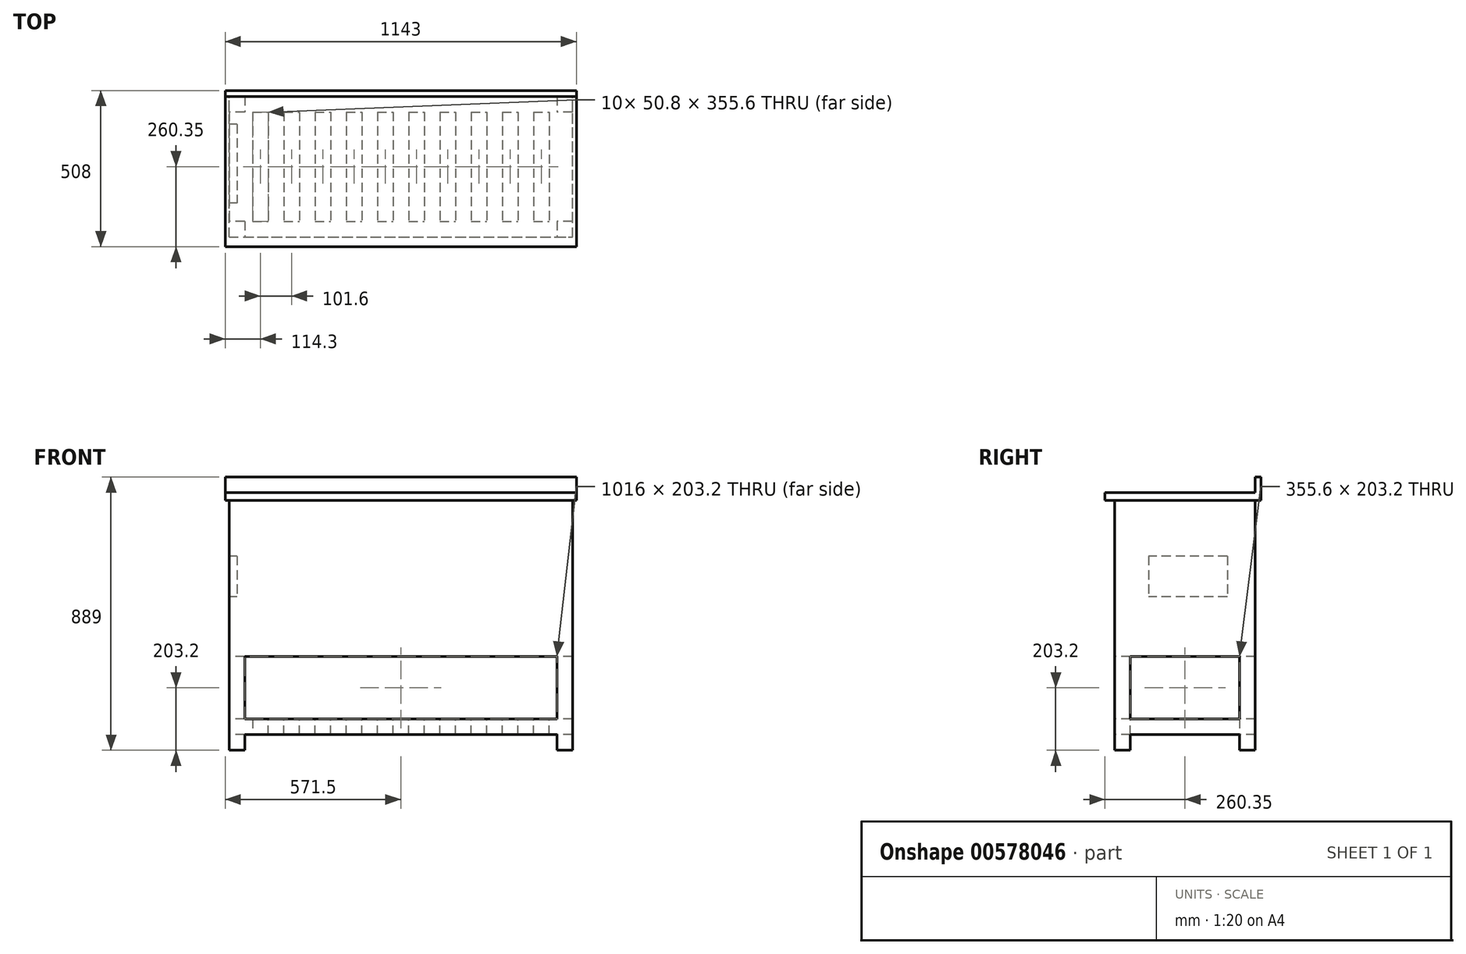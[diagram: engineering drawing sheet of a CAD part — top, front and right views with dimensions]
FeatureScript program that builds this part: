
annotation { "Feature Type Name" : "Feature", "Feature Type Description" : "" }
export const myFeature = defineFeature(function(context is Context, id is Id, definition is map)
    precondition{}
    {
        {
            var Q0;
            Q0=qCreatedBy(makeId("Front.planeOp"),FACE);
            var sketch = newSketch(context, id + "F0", { "sketchPlane" : qUnion([Q0])});
            skLineSegment(sketch, "E0.bottom", {"start": v(-558.8, 406.4) * mm, "end": v(558.8, 406.4) * mm});
            skLineSegment(sketch, "E0.top", {"start": v(-558.8, -406.4) * mm, "end": v(558.8, -406.4) * mm});
            skLineSegment(sketch, "E0.left", {"start": v(-558.8, 406.4) * mm, "end": v(-558.8, -406.4) * mm});
            skLineSegment(sketch, "E0.right", {"start": v(558.8, 406.4) * mm, "end": v(558.8, -406.4) * mm});
            skSolve(sketch);
        }
        {
            var Q0;
            Q0 = qSketchRegion(id + "F0", true);
            extrude(context, id + "F1", {"entities" : qUnion([Q0]), "depth" : 457.2 * mm, "offsetDistance" : 25.4 * mm});
        }
        {
            var Q0;
            Q0=makeQuery(id+"F1.opExtrude","CAP_FACE",FACE,{"disambiguationData":[OSD([sQuery(id+"F0.wireOp",EDGE,"E0.bottom"),sQuery(id+"F0.wireOp",EDGE,"E0.top"),sQuery(id+"F0.wireOp",EDGE,"E0.left"),sQuery(id+"F0.wireOp",EDGE,"E0.right")])],"isStart":false});
            var sketch = newSketch(context, id + "F2", { "sketchPlane" : qUnion([Q0])});
            skLineSegment(sketch, "E1.bottom", {"start": v(-558.8, 406.4) * mm, "end": v(-186.27, 406.4) * mm});
            skLineSegment(sketch, "E1.top", {"start": v(-558.8, -101.6) * mm, "end": v(-186.27, -101.6) * mm});
            skLineSegment(sketch, "E1.left", {"start": v(-558.8, 406.4) * mm, "end": v(-558.8, -101.6) * mm});
            skLineSegment(sketch, "E1.right", {"start": v(-186.27, 406.4) * mm, "end": v(-186.27, -101.6) * mm});
            skSolve(sketch);
        }
        {
            var Q0;
            {var subQ4=sQuery(id+"F2.wireOp",EDGE,"E1.top");Q0=makeQuery(id+"F2.imprint","IMPRINT",FACE,{"disambiguationData":[TD([[makeQuery(id+"F2.imprint","IMPRINT",EDGE,{"derivedFrom":subQ4}),-1.0]])]});}
            var sketch = newSketch(context, id + "F3", { "sketchPlane" : qUnion([Q0])});
            skLineSegment(sketch, "E2.bottom", {"start": v(-186.27, 406.4) * mm, "end": v(186.27, 406.4) * mm});
            skLineSegment(sketch, "E2.top", {"start": v(-186.27, -101.6) * mm, "end": v(186.27, -101.6) * mm});
            skLineSegment(sketch, "E2.left", {"start": v(-186.27, 406.4) * mm, "end": v(-186.27, -101.6) * mm});
            skLineSegment(sketch, "E2.right", {"start": v(186.27, 406.4) * mm, "end": v(186.27, -101.6) * mm});
            skSolve(sketch);
        }
        {
            var Q0;
            {var subQ4=sQuery(id+"F2.wireOp",EDGE,"E1.top");Q0=makeQuery(id+"F2.imprint","IMPRINT",FACE,{"disambiguationData":[TD([[makeQuery(id+"F2.imprint","IMPRINT",EDGE,{"derivedFrom":subQ4}),-1.0]])]});}
            var sketch = newSketch(context, id + "F4", { "sketchPlane" : qUnion([Q0])});
            skLineSegment(sketch, "E3.bottom", {"start": v(186.27, -101.6) * mm, "end": v(558.8, -101.6) * mm});
            skLineSegment(sketch, "E3.top", {"start": v(186.27, 152.4) * mm, "end": v(558.8, 152.4) * mm});
            skLineSegment(sketch, "E3.left", {"start": v(186.27, -101.6) * mm, "end": v(186.27, 152.4) * mm});
            skLineSegment(sketch, "E3.right", {"start": v(558.8, -101.6) * mm, "end": v(558.8, 152.4) * mm});
            skSolve(sketch);
        }
        {
            var Q0;
            {var subQ4=sQuery(id+"F2.wireOp",EDGE,"E1.top");Q0=makeQuery(id+"F2.imprint","IMPRINT",FACE,{"disambiguationData":[TD([[makeQuery(id+"F2.imprint","IMPRINT",EDGE,{"derivedFrom":subQ4}),-1.0]])]});}
            var sketch = newSketch(context, id + "F5", { "sketchPlane" : qUnion([Q0])});
            skLineSegment(sketch, "E4.bottom", {"start": v(186.27, 152.4) * mm, "end": v(558.8, 152.4) * mm});
            skLineSegment(sketch, "E4.top", {"start": v(186.27, 406.4) * mm, "end": v(558.8, 406.4) * mm});
            skLineSegment(sketch, "E4.left", {"start": v(186.27, 152.4) * mm, "end": v(186.27, 406.4) * mm});
            skLineSegment(sketch, "E4.right", {"start": v(558.8, 152.4) * mm, "end": v(558.8, 406.4) * mm});
            skSolve(sketch);
        }
        {
            var Q0;
            {var subQ4=sQuery(id+"F2.wireOp",EDGE,"E1.top");Q0=makeQuery(id+"F2.imprint","IMPRINT",FACE,{"disambiguationData":[TD([[makeQuery(id+"F2.imprint","IMPRINT",EDGE,{"derivedFrom":subQ4}),-1.0]])]});}
            var sketch = newSketch(context, id + "F6", { "sketchPlane" : qUnion([Q0])});
            skLineSegment(sketch, "E5.bottom", {"start": v(-508, -406.4) * mm, "end": v(508, -406.4) * mm});
            skLineSegment(sketch, "E5.top", {"start": v(-508, -355.6) * mm, "end": v(508, -355.6) * mm});
            skLineSegment(sketch, "E5.left", {"start": v(-508, -406.4) * mm, "end": v(-508, -355.6) * mm});
            skLineSegment(sketch, "E5.right", {"start": v(508, -406.4) * mm, "end": v(508, -355.6) * mm});
            skSolve(sketch);
        }
        {
            var Q0;
            Q0 = qSketchRegion(id + "F6", true);
            extrude(context, id + "F7", {"entities" : qUnion([Q0]), "operationType" : NewBodyOperationType.REMOVE, "oppositeDirection" : true, "depth" : 508 * mm, "offsetDistance" : 25.4 * mm});
        }
        {
            var Q0;
            {var subQ4=sQuery(id+"F2.wireOp",EDGE,"E1.top");Q0=makeQuery(id+"F2.imprint","IMPRINT",FACE,{"disambiguationData":[TD([[makeQuery(id+"F2.imprint","IMPRINT",EDGE,{"derivedFrom":subQ4}),-1.0]])]});}
            var sketch = newSketch(context, id + "F8", { "sketchPlane" : qUnion([Q0])});
            skLineSegment(sketch, "E6.bottom", {"start": v(-508, -304.8) * mm, "end": v(508, -304.8) * mm});
            skLineSegment(sketch, "E6.top", {"start": v(-508, -101.6) * mm, "end": v(508, -101.6) * mm});
            skLineSegment(sketch, "E6.left", {"start": v(-508, -304.8) * mm, "end": v(-508, -101.6) * mm});
            skLineSegment(sketch, "E6.right", {"start": v(508, -304.8) * mm, "end": v(508, -101.6) * mm});
            skSolve(sketch);
        }
        {
            var Q0;
            Q0 = qSketchRegion(id + "F8", true);
            extrude(context, id + "F9", {"entities" : qUnion([Q0]), "operationType" : NewBodyOperationType.REMOVE, "oppositeDirection" : true, "depth" : 508 * mm, "offsetDistance" : 25.4 * mm});
        }
        {
            var Q0;
            Q0=makeQuery(id+"F1.opExtrude","SWEPT_FACE",FACE,{"disambiguationData":[OSD([sQuery(id+"F0.wireOp",EDGE,"E0.left")])]});
            var sketch = newSketch(context, id + "F10", { "sketchPlane" : qUnion([Q0])});
            skLineSegment(sketch, "E7.bottom", {"start": v(50.8, -101.6) * mm, "end": v(406.4, -101.6) * mm});
            skLineSegment(sketch, "E7.top", {"start": v(50.8, -304.8) * mm, "end": v(406.4, -304.8) * mm});
            skLineSegment(sketch, "E7.left", {"start": v(50.8, -101.6) * mm, "end": v(50.8, -304.8) * mm});
            skLineSegment(sketch, "E7.right", {"start": v(406.4, -101.6) * mm, "end": v(406.4, -304.8) * mm});
            skSolve(sketch);
        }
        {
            var Q0;
            Q0 = qSketchRegion(id + "F10", true);
            extrude(context, id + "F11", {"entities" : qUnion([Q0]), "operationType" : NewBodyOperationType.REMOVE, "oppositeDirection" : true, "depth" : 1143 * mm, "offsetDistance" : 25.4 * mm});
        }
        {
            var Q0;
            Q0=makeQuery(id+"F1.opExtrude","SWEPT_FACE",FACE,{"disambiguationData":[OSD([sQuery(id+"F0.wireOp",EDGE,"E0.left")])]});
            var sketch = newSketch(context, id + "F12", { "sketchPlane" : qUnion([Q0])});
            skLineSegment(sketch, "E8.bottom", {"start": v(50.8, -406.4) * mm, "end": v(406.4, -406.4) * mm});
            skLineSegment(sketch, "E8.top", {"start": v(50.8, -355.6) * mm, "end": v(406.4, -355.6) * mm});
            skLineSegment(sketch, "E8.left", {"start": v(50.8, -406.4) * mm, "end": v(50.8, -355.6) * mm});
            skLineSegment(sketch, "E8.right", {"start": v(406.4, -406.4) * mm, "end": v(406.4, -355.6) * mm});
            skSolve(sketch);
        }
        {
            var Q0;
            Q0 = qSketchRegion(id + "F12", true);
            extrude(context, id + "F13", {"entities" : qUnion([Q0]), "operationType" : NewBodyOperationType.REMOVE, "oppositeDirection" : true, "depth" : 1143 * mm, "offsetDistance" : 25.4 * mm});
        }
        {
            var Q0;
            Q0=makeQuery(id+"F11.boolean.opBoolean","MERGE",FACE,{"derivedFrom":[makeQuery(id+"F9.boolean.opBoolean","COPY",FACE,{"derivedFrom":makeQuery(id+"F9.opExtrude","SWEPT_FACE",FACE,{"disambiguationData":[OSD([sQuery(id+"F8.wireOp",EDGE,"E6.bottom")])]})}),makeQuery(id+"F11.opExtrude","SWEPT_FACE",FACE,{"disambiguationData":[OSD([sQuery(id+"F10.wireOp",EDGE,"E7.top")])]})]});
            var sketch = newSketch(context, id + "F14", { "sketchPlane" : qUnion([Q0])});
            skLineSegment(sketch, "E9.bottom", {"start": v(-482.6, 0) * mm, "end": v(-431.8, 0) * mm});
            skLineSegment(sketch, "E9.top", {"start": v(-482.6, -457.2) * mm, "end": v(-431.8, -457.2) * mm});
            skLineSegment(sketch, "E9.left", {"start": v(-482.6, 0) * mm, "end": v(-482.6, -457.2) * mm});
            skLineSegment(sketch, "E9.right", {"start": v(-431.8, 0) * mm, "end": v(-431.8, -457.2) * mm});
            skLineSegment(sketch, "E10.bottom", {"start": v(-381, 0) * mm, "end": v(-330.2, 0) * mm});
            skLineSegment(sketch, "E10.top", {"start": v(-381, -457.2) * mm, "end": v(-330.2, -457.2) * mm});
            skLineSegment(sketch, "E10.left", {"start": v(-381, 0) * mm, "end": v(-381, -457.2) * mm});
            skLineSegment(sketch, "E10.right", {"start": v(-330.2, 0) * mm, "end": v(-330.2, -457.2) * mm});
            skLineSegment(sketch, "E11.bottom", {"start": v(-279.4, 0) * mm, "end": v(-228.6, 0) * mm});
            skLineSegment(sketch, "E11.top", {"start": v(-279.4, -457.2) * mm, "end": v(-228.6, -457.2) * mm});
            skLineSegment(sketch, "E11.left", {"start": v(-279.4, 0) * mm, "end": v(-279.4, -457.2) * mm});
            skLineSegment(sketch, "E11.right", {"start": v(-228.6, 0) * mm, "end": v(-228.6, -457.2) * mm});
            skLineSegment(sketch, "E12.bottom", {"start": v(-76.2, 0) * mm, "end": v(-25.4, 0) * mm});
            skLineSegment(sketch, "E12.top", {"start": v(-76.2, -457.2) * mm, "end": v(-25.4, -457.2) * mm});
            skLineSegment(sketch, "E12.left", {"start": v(-76.2, 0) * mm, "end": v(-76.2, -457.2) * mm});
            skLineSegment(sketch, "E12.right", {"start": v(-25.4, 0) * mm, "end": v(-25.4, -457.2) * mm});
            skLineSegment(sketch, "E13.bottom", {"start": v(25.4, 0) * mm, "end": v(76.2, 0) * mm});
            skLineSegment(sketch, "E13.top", {"start": v(25.4, -457.2) * mm, "end": v(76.2, -457.2) * mm});
            skLineSegment(sketch, "E13.left", {"start": v(25.4, 0) * mm, "end": v(25.4, -457.2) * mm});
            skLineSegment(sketch, "E13.right", {"start": v(76.2, 0) * mm, "end": v(76.2, -457.2) * mm});
            skLineSegment(sketch, "E14.bottom", {"start": v(127, 0) * mm, "end": v(177.8, 0) * mm});
            skLineSegment(sketch, "E14.top", {"start": v(127, -457.2) * mm, "end": v(177.8, -457.2) * mm});
            skLineSegment(sketch, "E14.left", {"start": v(127, 0) * mm, "end": v(127, -457.2) * mm});
            skLineSegment(sketch, "E14.right", {"start": v(177.8, 0) * mm, "end": v(177.8, -457.2) * mm});
            skLineSegment(sketch, "E15.bottom", {"start": v(228.6, 0) * mm, "end": v(279.4, 0) * mm});
            skLineSegment(sketch, "E15.top", {"start": v(228.6, -457.2) * mm, "end": v(279.4, -457.2) * mm});
            skLineSegment(sketch, "E15.left", {"start": v(228.6, 0) * mm, "end": v(228.6, -457.2) * mm});
            skLineSegment(sketch, "E15.right", {"start": v(279.4, 0) * mm, "end": v(279.4, -457.2) * mm});
            skLineSegment(sketch, "E16.bottom", {"start": v(330.2, 0) * mm, "end": v(381, 0) * mm});
            skLineSegment(sketch, "E16.top", {"start": v(330.2, -457.2) * mm, "end": v(381, -457.2) * mm});
            skLineSegment(sketch, "E16.left", {"start": v(330.2, 0) * mm, "end": v(330.2, -457.2) * mm});
            skLineSegment(sketch, "E16.right", {"start": v(381, 0) * mm, "end": v(381, -457.2) * mm});
            skLineSegment(sketch, "E17.bottom", {"start": v(431.8, 0) * mm, "end": v(482.6, 0) * mm});
            skLineSegment(sketch, "E17.top", {"start": v(431.8, -457.2) * mm, "end": v(482.6, -457.2) * mm});
            skLineSegment(sketch, "E17.left", {"start": v(431.8, 0) * mm, "end": v(431.8, -457.2) * mm});
            skLineSegment(sketch, "E17.right", {"start": v(482.6, 0) * mm, "end": v(482.6, -457.2) * mm});
            skPoint(sketch, "E18.oppositeSnap0", {"position": v(533.4, -406.4) * mm});
            skLineSegment(sketch, "E18.bottom", {"start": v(508, 0) * mm, "end": v(533.4, 0) * mm});
            skLineSegment(sketch, "E18.top", {"start": v(508, -457.2) * mm, "end": v(533.4, -457.2) * mm});
            skLineSegment(sketch, "E19.bottom", {"start": v(-177.8, 0) * mm, "end": v(-127, 0) * mm});
            skLineSegment(sketch, "E19.top", {"start": v(-177.8, -457.2) * mm, "end": v(-127, -457.2) * mm});
            skLineSegment(sketch, "E19.left", {"start": v(-177.8, 0) * mm, "end": v(-177.8, -457.2) * mm});
            skLineSegment(sketch, "E19.right", {"start": v(-127, 0) * mm, "end": v(-127, -457.2) * mm});
            skSolve(sketch);
        }
        {
            var Q0;
            Q0 = qSketchRegion(id + "F14", true);
            extrude(context, id + "F15", {"entities" : qUnion([Q0]), "operationType" : NewBodyOperationType.REMOVE, "oppositeDirection" : true, "depth" : 50.8 * mm, "offsetDistance" : 25.4 * mm});
        }
        {
            var Q0;
            Q0=makeQuery(id+"F1.opExtrude","SWEPT_FACE",FACE,{"disambiguationData":[OSD([sQuery(id+"F0.wireOp",EDGE,"E0.right")])]});
            var sketch = newSketch(context, id + "F16", { "sketchPlane" : qUnion([Q0])});
            skLineSegment(sketch, "E20.bottom", {"start": v(-457.2, -304.8) * mm, "end": v(-406.4, -304.8) * mm});
            skLineSegment(sketch, "E20.top", {"start": v(-457.2, -355.6) * mm, "end": v(-406.4, -355.6) * mm});
            skLineSegment(sketch, "E20.left", {"start": v(-457.2, -304.8) * mm, "end": v(-457.2, -355.6) * mm});
            skLineSegment(sketch, "E20.right", {"start": v(-406.4, -304.8) * mm, "end": v(-406.4, -355.6) * mm});
            skLineSegment(sketch, "E21.bottom", {"start": v(-50.8, -355.6) * mm, "end": v(0, -355.6) * mm});
            skLineSegment(sketch, "E21.top", {"start": v(-50.8, -304.8) * mm, "end": v(0, -304.8) * mm});
            skLineSegment(sketch, "E21.left", {"start": v(-50.8, -355.6) * mm, "end": v(-50.8, -304.8) * mm});
            skLineSegment(sketch, "E21.right", {"start": v(0, -355.6) * mm, "end": v(0, -304.8) * mm});
            skSolve(sketch);
        }
        {
            var Q0;
            Q0 = qSketchRegion(id + "F16", true);
            extrude(context, id + "F17", {"entities" : qUnion([Q0]), "operationType" : NewBodyOperationType.ADD, "oppositeDirection" : true, "depth" : 1117.6 * mm, "offsetDistance" : 25.4 * mm});
        }
        {
            var Q0;
            Q0=makeQuery(id+"F1.opExtrude","SWEPT_FACE",FACE,{"disambiguationData":[OSD([sQuery(id+"F0.wireOp",EDGE,"E0.left")])]});
            var sketch = newSketch(context, id + "F18", { "sketchPlane" : qUnion([Q0])});
            skLineSegment(sketch, "E22.bottom", {"start": v(90.66, 225.44) * mm, "end": v(346.7, 225.44) * mm});
            skLineSegment(sketch, "E22.top", {"start": v(90.66, 93.4) * mm, "end": v(346.7, 93.4) * mm});
            skLineSegment(sketch, "E22.left", {"start": v(90.66, 225.44) * mm, "end": v(90.66, 93.4) * mm});
            skLineSegment(sketch, "E22.right", {"start": v(346.7, 225.44) * mm, "end": v(346.7, 93.4) * mm});
            skSolve(sketch);
        }
        {
            var Q0;
            Q0=makeQuery(id+"F1.opExtrude","SWEPT_FACE",FACE,{"disambiguationData":[OSD([sQuery(id+"F0.wireOp",EDGE,"E0.bottom")])]});
            var sketch = newSketch(context, id + "F19", { "sketchPlane" : qUnion([Q0])});
            skLineSegment(sketch, "E23.bottom", {"start": v(-571.5, 19.05) * mm, "end": v(571.5, 19.05) * mm});
            skLineSegment(sketch, "E23.top", {"start": v(-571.5, -488.95) * mm, "end": v(571.5, -488.95) * mm});
            skLineSegment(sketch, "E23.left", {"start": v(-571.5, 19.05) * mm, "end": v(-571.5, -488.95) * mm});
            skLineSegment(sketch, "E23.right", {"start": v(571.5, 19.05) * mm, "end": v(571.5, -488.95) * mm});
            skSolve(sketch);
        }
        {
            var Q0;
            Q0 = qSketchRegion(id + "F19", true);
            extrude(context, id + "F20", {"entities" : qUnion([Q0]), "operationType" : NewBodyOperationType.ADD, "depth" : 25.4 * mm, "offsetDistance" : 25.4 * mm});
        }
        {
            var Q0;
            Q0=makeQuery(id+"F20.opExtrude","CAP_FACE",FACE,{"disambiguationData":[OSD([sQuery(id+"F19.wireOp",EDGE,"E23.bottom"),sQuery(id+"F19.wireOp",EDGE,"E23.top"),sQuery(id+"F19.wireOp",EDGE,"E23.left"),sQuery(id+"F19.wireOp",EDGE,"E23.right")])],"isStart":false});
            var sketch = newSketch(context, id + "F21", { "sketchPlane" : qUnion([Q0])});
            skLineSegment(sketch, "E24.bottom", {"start": v(-419.57, -88.9) * mm, "end": v(47.03, -88.9) * mm});
            skLineSegment(sketch, "E24.top", {"start": v(-419.57, -409.45) * mm, "end": v(47.03, -409.45) * mm});
            skLineSegment(sketch, "E24.left", {"start": v(-419.57, -88.9) * mm, "end": v(-419.57, -409.45) * mm});
            skLineSegment(sketch, "E24.right", {"start": v(47.03, -88.9) * mm, "end": v(47.03, -409.45) * mm});
            skSolve(sketch);
        }
        {
            var Q0;
            Q0 = qSketchRegion(id + "F18", true);
            extrude(context, id + "F22", {"entities" : qUnion([Q0]), "operationType" : NewBodyOperationType.REMOVE, "oppositeDirection" : true, "depth" : 25.4 * mm, "offsetDistance" : 25.4 * mm});
        }
        {
            var Q0;
            Q0=makeQuery(id+"F20.opExtrude","CAP_FACE",FACE,{"disambiguationData":[OSD([sQuery(id+"F19.wireOp",EDGE,"E23.bottom"),sQuery(id+"F19.wireOp",EDGE,"E23.top"),sQuery(id+"F19.wireOp",EDGE,"E23.left"),sQuery(id+"F19.wireOp",EDGE,"E23.right")])],"isStart":false});
            var sketch = newSketch(context, id + "F23", { "sketchPlane" : qUnion([Q0])});
            skLineSegment(sketch, "E25.bottom", {"start": v(-571.5, 19.05) * mm, "end": v(571.5, 19.05) * mm});
            skLineSegment(sketch, "E25.top", {"start": v(-571.5, 0) * mm, "end": v(571.5, 0) * mm});
            skLineSegment(sketch, "E25.left", {"start": v(-571.5, 19.05) * mm, "end": v(-571.5, 0) * mm});
            skLineSegment(sketch, "E25.right", {"start": v(571.5, 19.05) * mm, "end": v(571.5, 0) * mm});
            skSolve(sketch);
        }
        {
            var Q0;
            Q0 = qSketchRegion(id + "F23", true);
            extrude(context, id + "F24", {"entities" : qUnion([Q0]), "operationType" : NewBodyOperationType.ADD, "depth" : 50.8 * mm, "offsetDistance" : 25.4 * mm});
        }
    });
